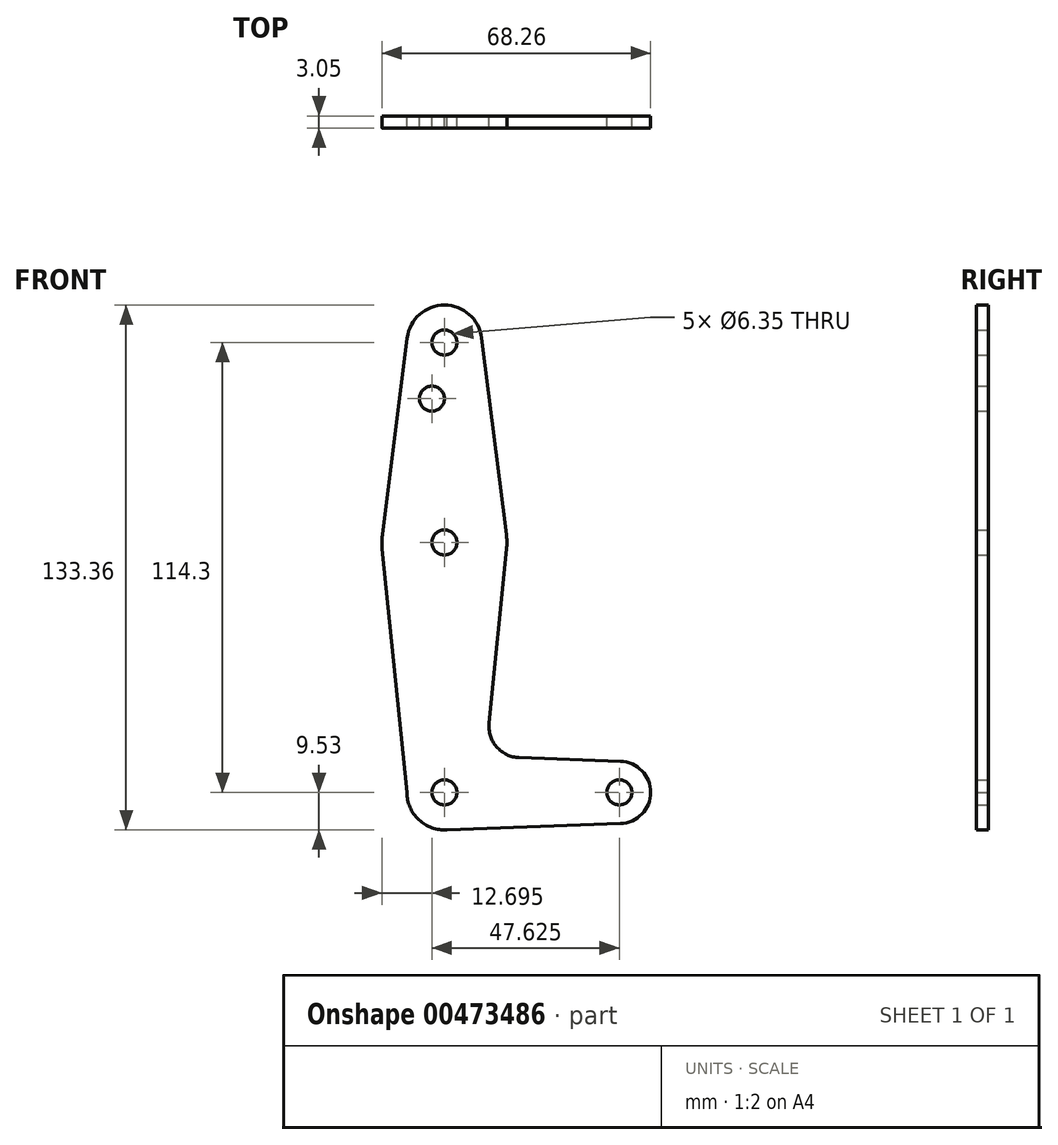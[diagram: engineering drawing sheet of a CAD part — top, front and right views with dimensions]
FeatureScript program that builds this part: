
annotation { "Feature Type Name" : "Feature", "Feature Type Description" : "" }
export const myFeature = defineFeature(function(context is Context, id is Id, definition is map)
    precondition{}
    {
        {
            var Q0;
            Q0=qCreatedBy(makeId("Front.planeOp"),FACE);
            var sketch = newSketch(context, id + "F0", { "sketchPlane" : qUnion([Q0])});
            skLineSegment(sketch, "E0", {"start": v(0, 114.3) * mm, "end": v(0, 0) * mm, "construction": true});
            skLineSegment(sketch, "E1", {"start": v(0, 0) * mm, "end": v(44.45, 0) * mm, "construction": true});
            skCircle(sketch, "E2", {"center": v(0, 114.3) * mm, "radius": 9.53 * mm});
            skCircle(sketch, "E3", {"center": v(0, 0) * mm, "radius": 9.53 * mm});
            skCircle(sketch, "E4", {"center": v(44.45, 0) * mm, "radius": 7.94 * mm});
            skCircle(sketch, "E5", {"center": v(0, 63.5) * mm, "radius": 15.88 * mm});
            skLineSegment(sketch, "E6", {"start": v(-9.45, 115.5) * mm, "end": v(-15.75, 65.48) * mm});
            skLineSegment(sketch, "E7", {"start": v(9.45, 115.5) * mm, "end": v(15.75, 65.48) * mm});
            skLineSegment(sketch, "E8", {"start": v(-15.8, 61.9) * mm, "end": v(-9.52, 0) * mm});
            skLineSegment(sketch, "E9", {"start": v(15.8, 61.9) * mm, "end": v(11.34, 17.59) * mm});
            skLineSegment(sketch, "E10", {"start": v(0, -9.53) * mm, "end": v(44.73, -7.93) * mm});
            skLineSegment(sketch, "E11", {"start": v(18.97, 8.85) * mm, "end": v(44.73, 7.93) * mm});
            skCircle(sketch, "E12", {"center": v(0, 114.3) * mm, "radius": 3.18 * mm});
            skCircle(sketch, "E13", {"center": v(0, 63.5) * mm, "radius": 3.18 * mm});
            skCircle(sketch, "E14", {"center": v(0, 0) * mm, "radius": 3.18 * mm});
            skCircle(sketch, "E15", {"center": v(44.45, 0) * mm, "radius": 3.18 * mm});
            skArc(sketch, "E16.filletArc", {"start": v(11.34, 17.59) * mm, "mid": v(13.26, 11.57) * mm, "end": v(18.97, 8.85) * mm});
            skCircle(sketch, "E17", {"center": v(-3.17, 100.03) * mm, "radius": 3.18 * mm});
            skSolve(sketch);
        }
        {
            var Q0;
            Q0 = qSketchRegion(id + "F0", true);
            extrude(context, id + "F1", {"entities" : qUnion([Q0]), "depth" : 3.05 * mm});
        }
    });
